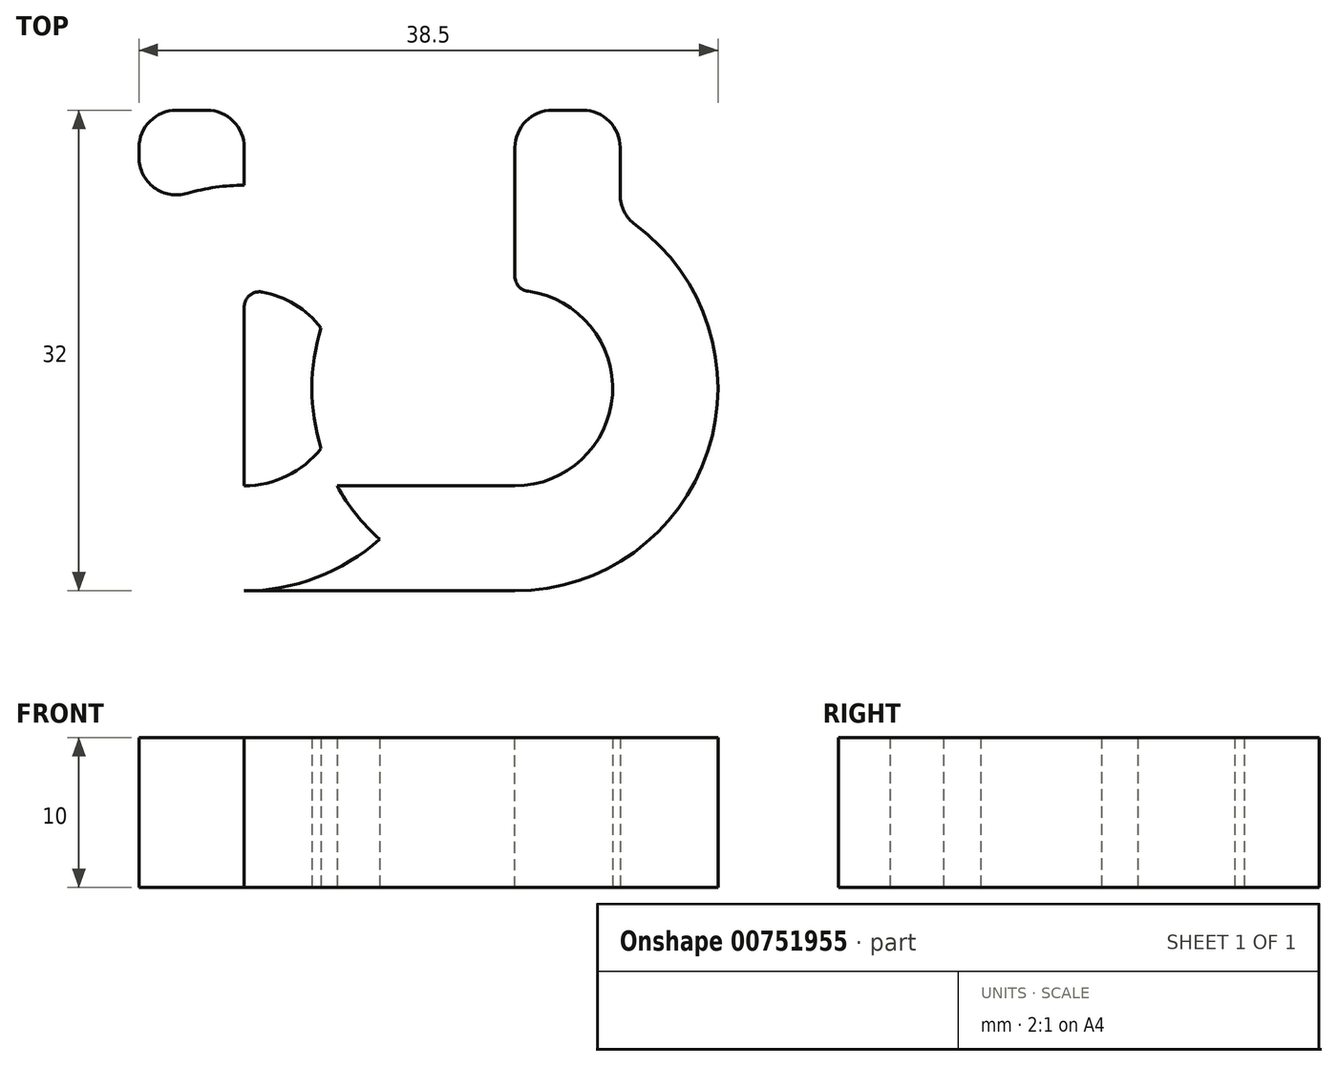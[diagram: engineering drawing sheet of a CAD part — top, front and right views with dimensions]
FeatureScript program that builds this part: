
annotation { "Feature Type Name" : "Feature", "Feature Type Description" : "" }
export const myFeature = defineFeature(function(context is Context, id is Id, definition is map)
    precondition{}
    {
        {
            var Q0;
            Q0=qCreatedBy(makeId("Top.planeOp"),FACE);
            var sketch = newSketch(context, id + "F0", { "sketchPlane" : qUnion([Q0])});
            skCircle(sketch, "E0", {"center": v(9, 0) * mm, "radius": 6.5 * mm});
            skCircle(sketch, "E1.MirrorC", {"center": v(-9, 0) * mm, "radius": 6.5 * mm});
            skLineSegment(sketch, "E2", {"start": v(9, 18.5) * mm, "end": v(9, -6.5) * mm});
            skLineSegment(sketch, "E3.MirrorCS", {"start": v(-9, 18.5) * mm, "end": v(-9, -6.5) * mm});
            skLineSegment(sketch, "E4", {"start": v(-9, -6.5) * mm, "end": v(9, -6.5) * mm});
            skCircle(sketch, "E5.0", {"center": v(-9, 0) * mm, "radius": 13.5 * mm});
            skCircle(sketch, "E6.0", {"center": v(9, 0) * mm, "radius": 13.5 * mm});
            skLineSegment(sketch, "E7", {"start": v(9, -13.5) * mm, "end": v(-9, -13.5) * mm});
            skLineSegment(sketch, "E8", {"start": v(9, 18.5) * mm, "end": v(16, 18.5) * mm});
            skLineSegment(sketch, "E9", {"start": v(16, 18.5) * mm, "end": v(16, 11.54) * mm});
            skLineSegment(sketch, "E10.MirrorCS", {"start": v(-9, 18.5) * mm, "end": v(-16, 18.5) * mm});
            skLineSegment(sketch, "E11.MirrorCS", {"start": v(-16, 18.5) * mm, "end": v(-16, 11.54) * mm});
            skSolve(sketch);
        }
        {
            var Q0;
            {var subQ0=sQuery(id+"F0.wireOp",EDGE,"E10.MirrorCS");Q0=makeQuery(id+"F0.imprint","IMPRINT",FACE,{"disambiguationData":[TD([[makeQuery(id+"F0.imprint","IMPRINT",EDGE,{"derivedFrom":subQ0}),1.0]])]});}
            var Q1;
            {var subQ1=sQuery(id+"F0.wireOp",EDGE,"E1.MirrorC");var subQ6=sQuery(id+"F0.wireOp",EDGE,"E3.MirrorCS");var subQ11=makeQuery(id+"F0.imprint","INTERSECT",VERTEX,{"disambiguationData":[OD(0.0)],"derivedFrom":[subQ1,subQ6]});Q1=makeQuery(id+"F0.imprint","IMPRINT",FACE,{"disambiguationData":[TD([[makeQuery(id+"F0.imprint","IMPRINT",EDGE,{"disambiguationData":[TD([[subQ11,1.0]])],"derivedFrom":subQ1}),1.0]])]});}
            var Q2;
            {var subQ0=sQuery(id+"F0.wireOp",EDGE,"E6.0");var subQ1=sQuery(id+"F0.wireOp",EDGE,"E4");var subQ2=makeQuery(id+"F0.imprint","INTERSECT",VERTEX,{"derivedFrom":[subQ1,subQ0]});Q2=makeQuery(id+"F0.imprint","IMPRINT",FACE,{"disambiguationData":[TD([[makeQuery(id+"F0.imprint","IMPRINT",EDGE,{"disambiguationData":[TD([[subQ2,-1.0]])],"derivedFrom":subQ1}),-1.0]])]});}
            var Q3;
            {var subQ1=sQuery(id+"F0.wireOp",EDGE,"E2");var subQ3=sQuery(id+"F0.wireOp",EDGE,"E0");var subQ8=makeQuery(id+"F0.imprint","INTERSECT",VERTEX,{"disambiguationData":[OD(0.0)],"derivedFrom":[subQ3,subQ1]});Q3=makeQuery(id+"F0.imprint","IMPRINT",FACE,{"disambiguationData":[TD([[makeQuery(id+"F0.imprint","IMPRINT",EDGE,{"disambiguationData":[TD([[subQ8,1.0]])],"derivedFrom":subQ3}),-1.0]])]});}
            var Q4;
            {var subQ0=sQuery(id+"F0.wireOp",EDGE,"E7");Q4=makeQuery(id+"F0.imprint","IMPRINT",FACE,{"disambiguationData":[TD([[makeQuery(id+"F0.imprint","IMPRINT",EDGE,{"derivedFrom":subQ0}),-1.0]])]});}
            var Q5;
            {var subQ0=sQuery(id+"F0.wireOp",EDGE,"E8");Q5=makeQuery(id+"F0.imprint","IMPRINT",FACE,{"disambiguationData":[TD([[makeQuery(id+"F0.imprint","IMPRINT",EDGE,{"derivedFrom":subQ0}),-1.0]])]});}
            extrude(context, id + "F1", {"entities" : qUnion([Q0, Q1, Q2, Q3, Q4, Q5]), "depth" : 10 * mm, "offsetDistance" : 25 * mm});
        }
        {
            var Q0;
            Q0=makeQuery(id+"F1.opExtrude","SWEPT_EDGE",EDGE,{"disambiguationData":[OSD([sQuery(id+"F0.wireOp",EDGE,"E8"),sQuery(id+"F0.wireOp",EDGE,"E9")])]});
            var Q1;
            Q1=makeQuery(id+"F1.opExtrude","SWEPT_EDGE",EDGE,{"disambiguationData":[OSD([sQuery(id+"F0.wireOp",EDGE,"E2"),sQuery(id+"F0.wireOp",EDGE,"E8")])]});
            var Q2;
            Q2=makeQuery(id+"F1.opExtrude","SWEPT_EDGE",EDGE,{"disambiguationData":[OSD([sQuery(id+"F0.wireOp",EDGE,"E3.MirrorCS"),sQuery(id+"F0.wireOp",EDGE,"E10.MirrorCS")])]});
            var Q3;
            Q3=makeQuery(id+"F1.opExtrude","SWEPT_EDGE",EDGE,{"disambiguationData":[OSD([sQuery(id+"F0.wireOp",EDGE,"E10.MirrorCS"),sQuery(id+"F0.wireOp",EDGE,"E11.MirrorCS")])]});
            var Q4;
            Q4=makeQuery(id+"F1.opExtrude","SWEPT_EDGE",EDGE,{"disambiguationData":[OSD([sQuery(id+"F0.wireOp",EDGE,"E6.0"),sQuery(id+"F0.wireOp",EDGE,"E9")])]});
            var Q5;
            Q5=makeQuery(id+"F1.opExtrude","SWEPT_EDGE",EDGE,{"disambiguationData":[OSD([sQuery(id+"F0.wireOp",EDGE,"E5.0"),sQuery(id+"F0.wireOp",EDGE,"E11.MirrorCS")])]});
            fillet(context, id + "F2", {"entities" : qUnion([Q0, Q1, Q2, Q3, Q4, Q5]), "radius" : 2.5 * mm, "tangentPropagation" : true, "allowEdgeOverflow" : false});
        }
        {
            var Q0;
            Q0=makeQuery(id+"F1.opExtrude","SWEPT_EDGE",EDGE,{"disambiguationData":[OSD([sQuery(id+"F0.wireOp",EDGE,"E1.MirrorC"),sQuery(id+"F0.wireOp",EDGE,"E3.MirrorCS")])]});
            var Q1;
            Q1=makeQuery(id+"F1.opExtrude","SWEPT_EDGE",EDGE,{"disambiguationData":[OSD([sQuery(id+"F0.wireOp",EDGE,"E0"),sQuery(id+"F0.wireOp",EDGE,"E2")])]});
            fillet(context, id + "F3", {"entities" : qUnion([Q0, Q1]), "radius" : 1 * mm, "tangentPropagation" : true, "allowEdgeOverflow" : false});
        }
    });
